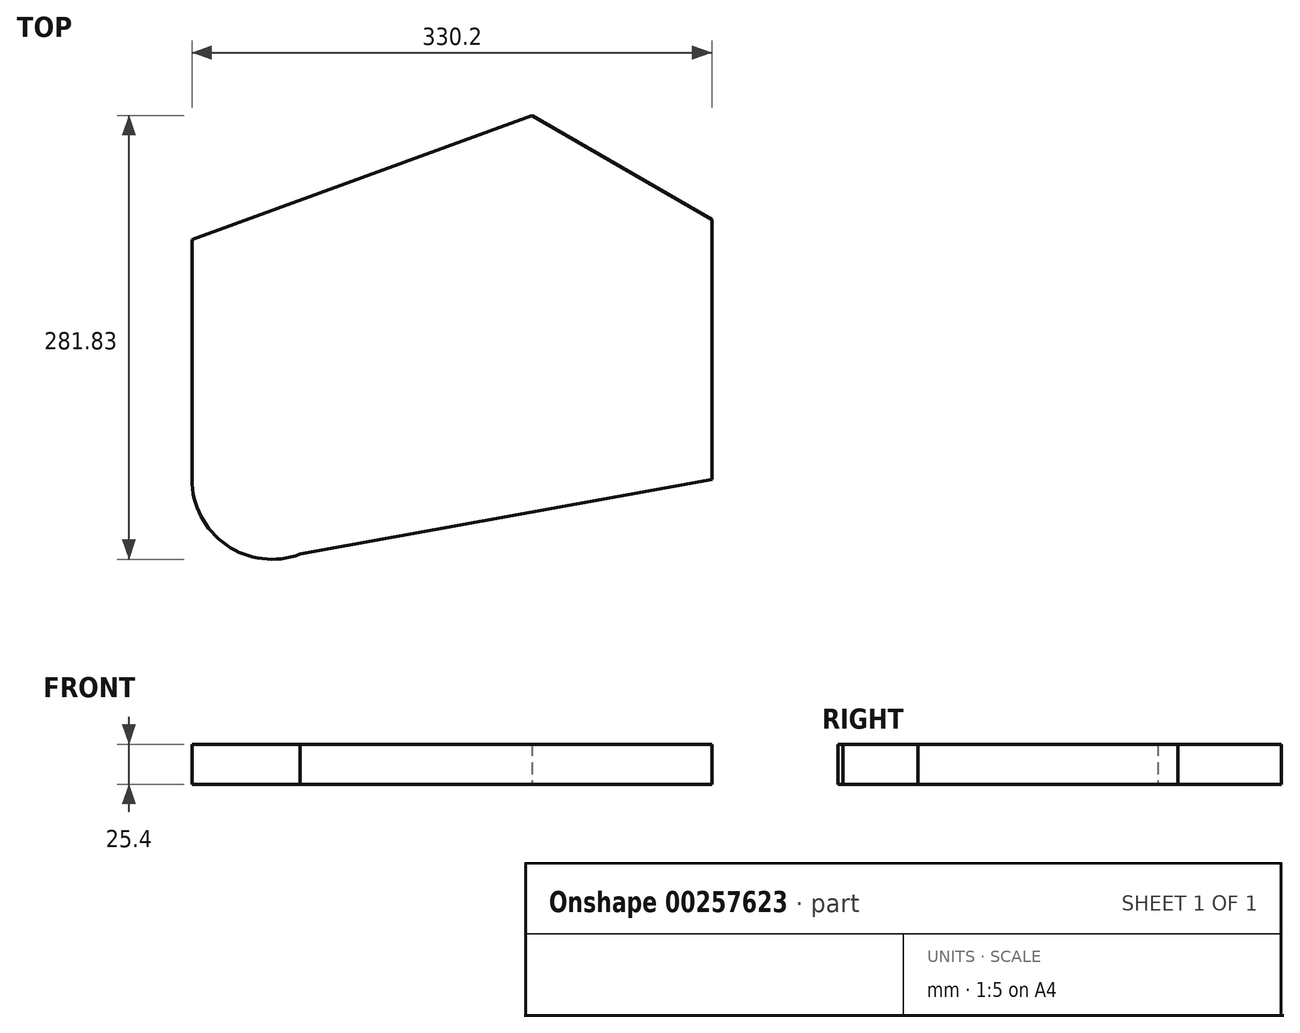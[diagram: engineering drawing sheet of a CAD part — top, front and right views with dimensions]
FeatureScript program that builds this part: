
annotation { "Feature Type Name" : "Feature", "Feature Type Description" : "" }
export const myFeature = defineFeature(function(context is Context, id is Id, definition is map)
    precondition{}
    {
        {
            var Q0;
            Q0=qCreatedBy(makeId("Top.planeOp"),FACE);
            var sketch = newSketch(context, id + "F0", { "sketchPlane" : qUnion([Q0])});
            skLineSegment(sketch, "E0", {"start": v(295.52, -65.32) * mm, "end": v(295.52, 99.78) * mm});
            skArc(sketch, "E1", {"start": v(-34.68, -65.32) * mm, "mid": v(-12.8, -107.08) * mm, "end": v(34, -112.87) * mm});
            skLineSegment(sketch, "E2", {"start": v(16.12, -116.12) * mm, "end": v(295.52, -65.32) * mm});
            skLineSegment(sketch, "E3", {"start": v(-34.68, -65.32) * mm, "end": v(-34.68, 87.08) * mm});
            skLineSegment(sketch, "E4", {"start": v(295.52, 99.78) * mm, "end": v(181.34, 165.7) * mm});
            skLineSegment(sketch, "E5", {"start": v(181.34, 165.7) * mm, "end": v(-34.68, 87.08) * mm});
            skSolve(sketch);
        }
        {
            var Q0;
            Q0 = qSketchRegion(id + "F0", true);
            extrude(context, id + "F1", {"entities" : qUnion([Q0]), "depth" : 25.4 * mm});
        }
    });
